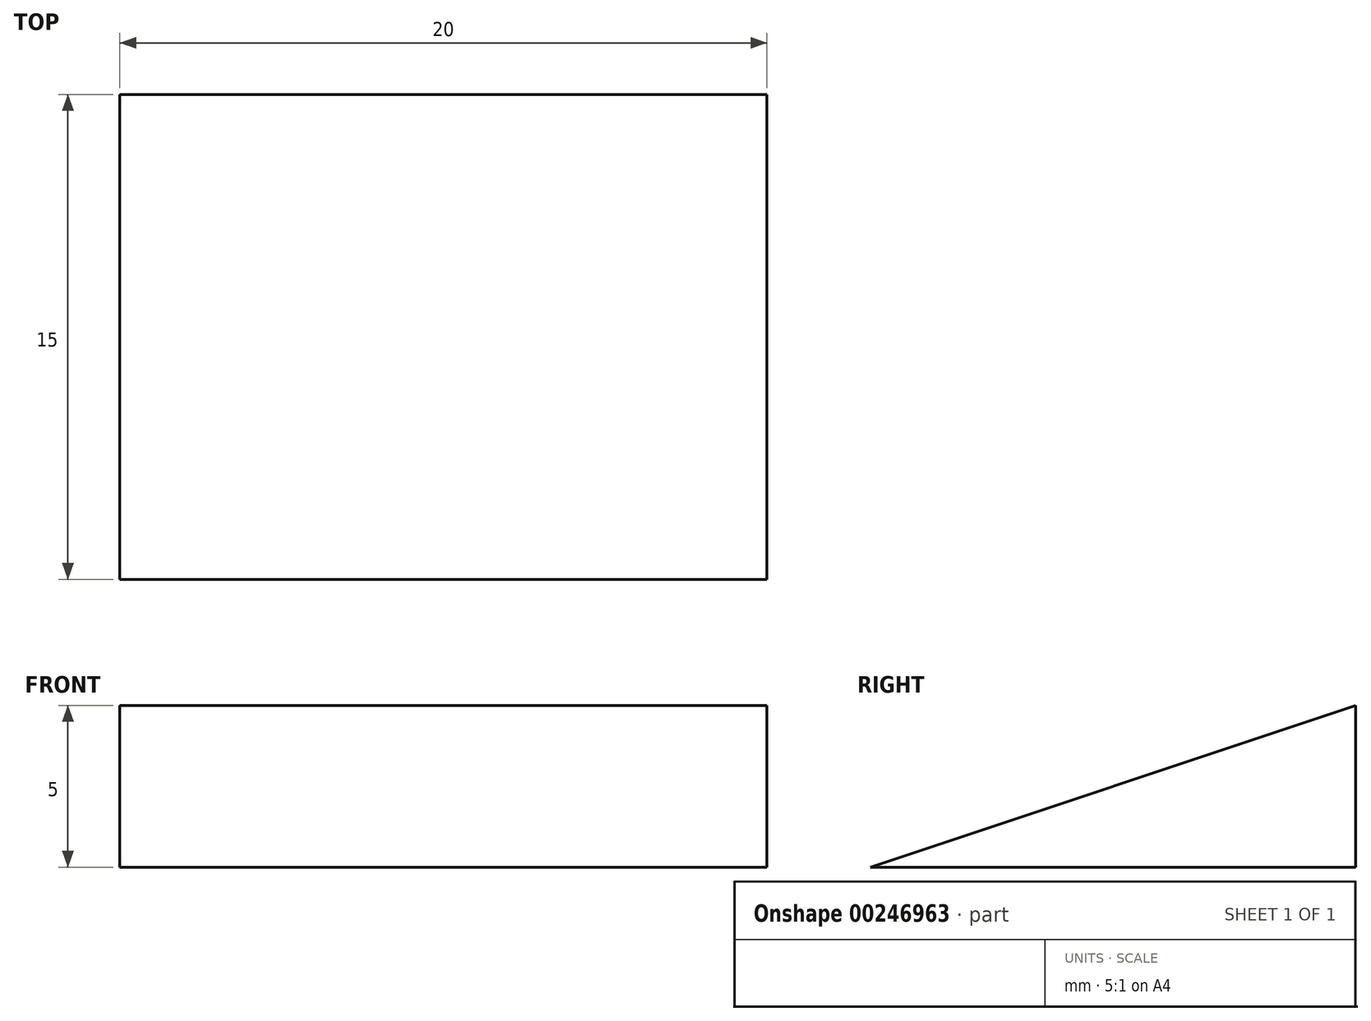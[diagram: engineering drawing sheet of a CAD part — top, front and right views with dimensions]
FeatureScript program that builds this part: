
annotation { "Feature Type Name" : "Feature", "Feature Type Description" : "" }
export const myFeature = defineFeature(function(context is Context, id is Id, definition is map)
    precondition{}
    {
        {
            var Q0;
            Q0=qCreatedBy(makeId("Right.planeOp"),FACE);
            var sketch = newSketch(context, id + "F0", { "sketchPlane" : qUnion([Q0])});
            skLineSegment(sketch, "E0.bottom", {"start": v(0, 0) * mm, "end": v(15, 0) * mm});
            skLineSegment(sketch, "E0.right", {"start": v(15, 0) * mm, "end": v(15, 5) * mm});
            skLineSegment(sketch, "E1", {"start": v(15, 5) * mm, "end": v(0, 0) * mm});
            skSolve(sketch);
        }
        {
            var Q0;
            Q0=makeQuery(id+"F0.imprint","IMPRINT",FACE,{"disambiguationData":[TD([[makeQuery(id+"F0.imprint","IMPRINT",EDGE,{"derivedFrom":sQuery(id+"F0.wireOp",EDGE,"E0.bottom")}),1.0]])]});
            extrude(context, id + "F1", {"entities" : qUnion([Q0]), "depth" : 20 * mm});
        }
    });
